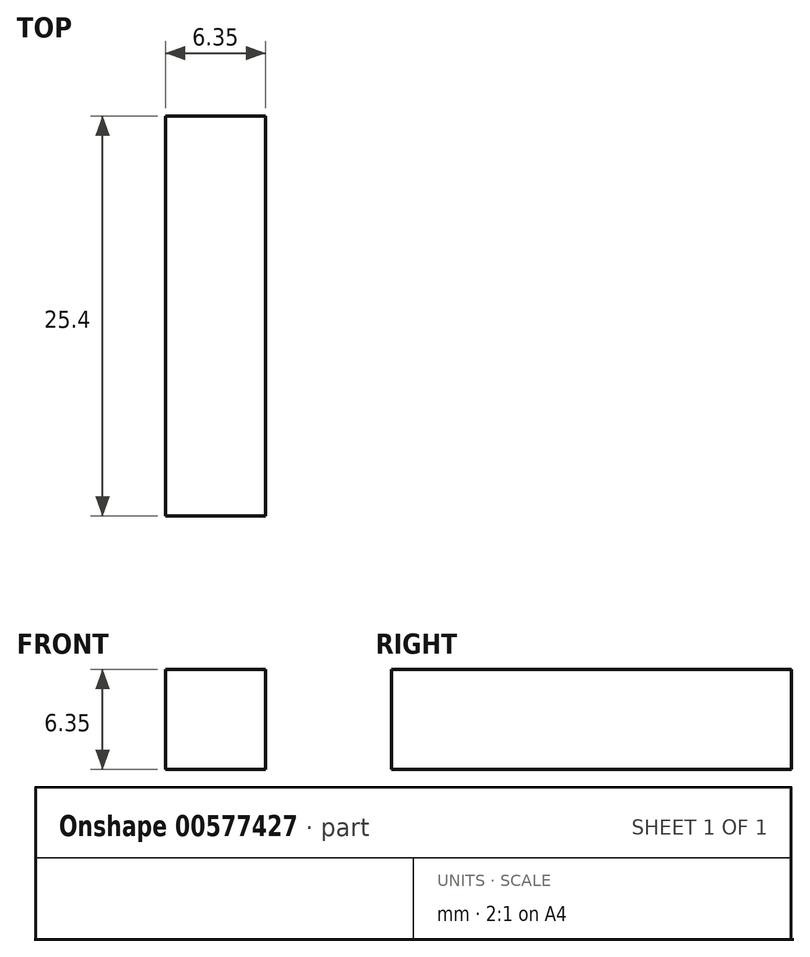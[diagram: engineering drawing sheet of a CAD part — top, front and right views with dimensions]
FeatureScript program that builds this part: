
annotation { "Feature Type Name" : "Feature", "Feature Type Description" : "" }
export const myFeature = defineFeature(function(context is Context, id is Id, definition is map)
    precondition{}
    {
        {
            var Q0;
            Q0=qCreatedBy(makeId("Front.planeOp"),FACE);
            var sketch = newSketch(context, id + "F0", { "sketchPlane" : qUnion([Q0])});
            skLineSegment(sketch, "E0.bottom", {"start": v(0, 0) * mm, "end": v(6.35, 0) * mm});
            skLineSegment(sketch, "E0.top", {"start": v(0, 6.35) * mm, "end": v(6.35, 6.35) * mm});
            skLineSegment(sketch, "E0.left", {"start": v(0, 0) * mm, "end": v(0, 6.35) * mm});
            skLineSegment(sketch, "E0.right", {"start": v(6.35, 0) * mm, "end": v(6.35, 6.35) * mm});
            skSolve(sketch);
        }
        {
            var Q0;
            Q0=makeQuery(id+"F0.imprint","IMPRINT",FACE,{"disambiguationData":[TD([[makeQuery(id+"F0.imprint","IMPRINT",EDGE,{"derivedFrom":sQuery(id+"F0.wireOp",EDGE,"E0.bottom")}),1.0]])]});
            extrude(context, id + "F1", {"entities" : qUnion([Q0]), "depth" : 25.4 * mm, "offsetDistance" : 25.4 * mm});
        }
    });
